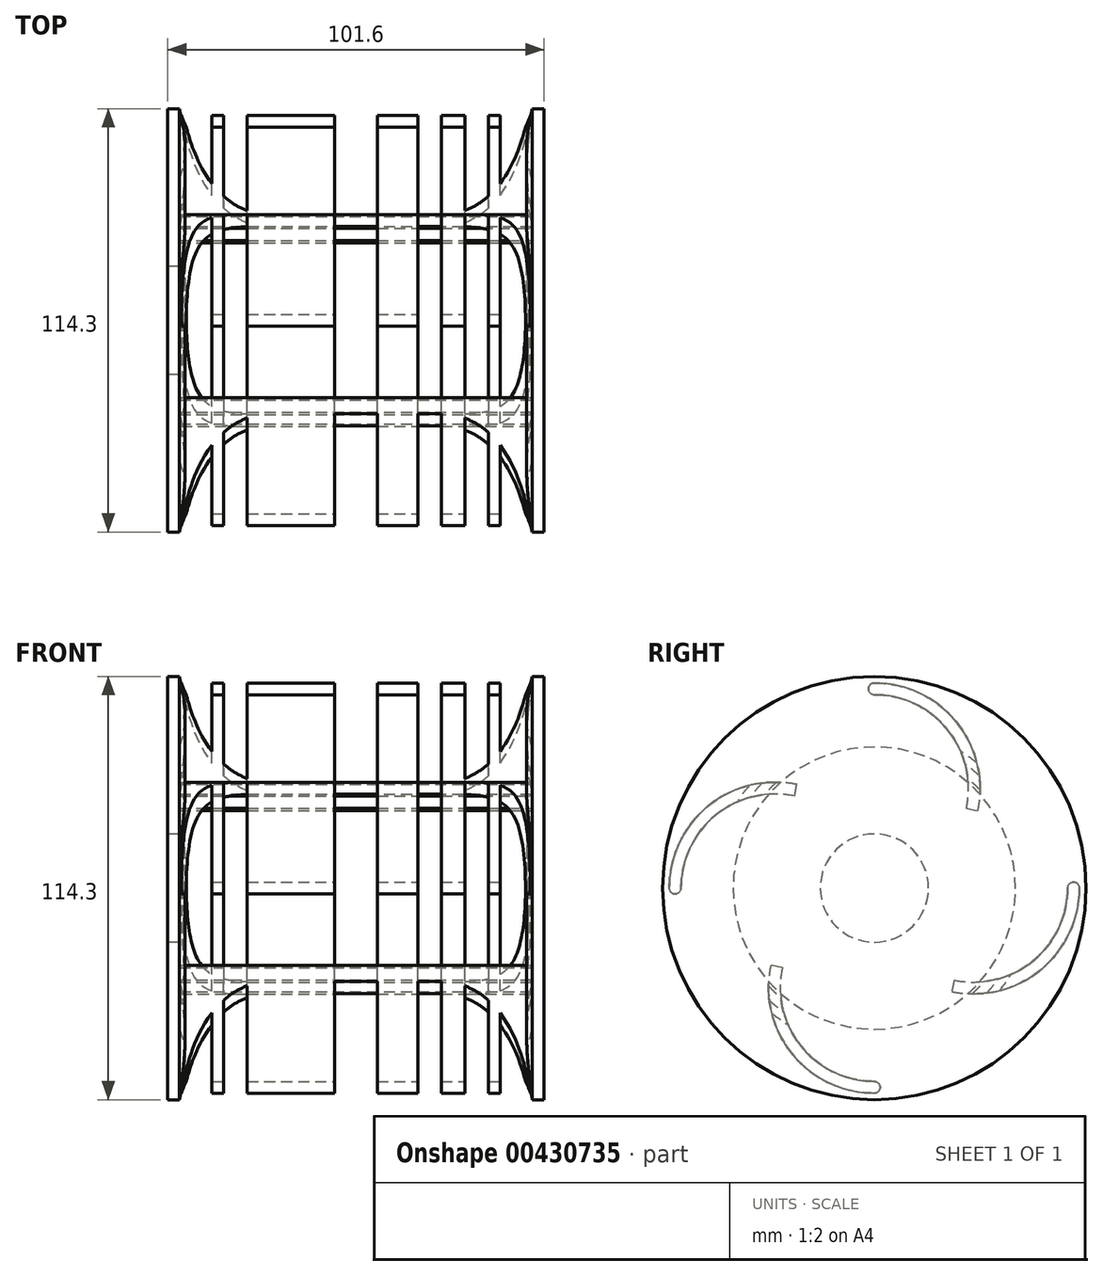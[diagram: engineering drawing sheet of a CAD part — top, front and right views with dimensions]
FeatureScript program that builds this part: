
annotation { "Feature Type Name" : "Feature", "Feature Type Description" : "" }
export const myFeature = defineFeature(function(context is Context, id is Id, definition is map)
    precondition{}
    {
        {
            var Q0;
            Q0=qCreatedBy(makeId("Front.planeOp"),FACE);
            var sketch = newSketch(context, id + "F0", { "sketchPlane" : qUnion([Q0])});
            skLineSegment(sketch, "E0.bottom", {"start": v(0, 0) * mm, "end": v(-101.6, 0) * mm});
            skLineSegment(sketch, "E0.top", {"start": v(0, 38.1) * mm, "end": v(-101.6, 38.1) * mm});
            skLineSegment(sketch, "E0.left", {"start": v(0, 0) * mm, "end": v(0, 38.1) * mm});
            skLineSegment(sketch, "E0.right", {"start": v(-101.6, 0) * mm, "end": v(-101.6, 38.1) * mm});
            skLineSegment(sketch, "E1.bottom", {"start": v(-3.18, 0) * mm, "end": v(0, 0) * mm});
            skLineSegment(sketch, "E1.top", {"start": v(-3.18, 57.15) * mm, "end": v(0, 57.15) * mm});
            skLineSegment(sketch, "E1.left", {"start": v(0, 0) * mm, "end": v(0, 57.15) * mm});
            skLineSegment(sketch, "E1.right", {"start": v(-3.18, 0) * mm, "end": v(-3.18, 57.15) * mm});
            skLineSegment(sketch, "E2.bottom", {"start": v(-101.6, 0) * mm, "end": v(-98.43, 0) * mm});
            skLineSegment(sketch, "E2.top", {"start": v(-101.6, 57.15) * mm, "end": v(-98.43, 57.15) * mm});
            skLineSegment(sketch, "E2.left", {"start": v(-101.6, 0) * mm, "end": v(-101.6, 57.15) * mm});
            skLineSegment(sketch, "E2.right", {"start": v(-98.43, 0) * mm, "end": v(-98.43, 57.15) * mm});
            skLineSegment(sketch, "E3", {"start": v(-98.43, 57.15) * mm, "end": v(-94.62, 38.1) * mm});
            skLineSegment(sketch, "E4", {"start": v(-98.43, 57.15) * mm, "end": v(-98.43, 38.1) * mm});
            skLineSegment(sketch, "E5", {"start": v(-98.43, 38.1) * mm, "end": v(-94.62, 38.1) * mm});
            skLineSegment(sketch, "E6", {"start": v(-3.18, 57.15) * mm, "end": v(-6.99, 38.1) * mm});
            skSolve(sketch);
        }
        {
            var Q0;
            {var subQ0=sQuery(id+"F0.wireOp",EDGE,"E0.bottom");Q0=makeQuery(id+"F0.imprint","IMPRINT",FACE,{"disambiguationData":[TD([[makeQuery(id+"F0.imprint","IMPRINT",EDGE,{"derivedFrom":subQ0}),-1.0]])]});}
            var Q1;
            {var subQ5=sQuery(id+"F0.wireOp",EDGE,"E1.bottom");Q1=makeQuery(id+"F0.imprint","IMPRINT",FACE,{"disambiguationData":[TD([[makeQuery(id+"F0.imprint","IMPRINT",EDGE,{"derivedFrom":subQ5}),1.0]])]});}
            var Q2;
            {var subQ5=sQuery(id+"F0.wireOp",EDGE,"E1.top");Q2=makeQuery(id+"F0.imprint","IMPRINT",FACE,{"disambiguationData":[TD([[makeQuery(id+"F0.imprint","IMPRINT",EDGE,{"derivedFrom":subQ5}),-1.0]])]});}
            var Q3;
            {var subQ5=sQuery(id+"F0.wireOp",EDGE,"E2.top");Q3=makeQuery(id+"F0.imprint","IMPRINT",FACE,{"disambiguationData":[TD([[makeQuery(id+"F0.imprint","IMPRINT",EDGE,{"derivedFrom":subQ5}),-1.0]])]});}
            var Q4;
            {var subQ5=sQuery(id+"F0.wireOp",EDGE,"E2.bottom");Q4=makeQuery(id+"F0.imprint","IMPRINT",FACE,{"disambiguationData":[TD([[makeQuery(id+"F0.imprint","IMPRINT",EDGE,{"derivedFrom":subQ5}),1.0]])]});}
            var Q5;
            Q5=makeQuery(id+"F0.imprint","IMPRINT",FACE,{"disambiguationData":[TD([[makeQuery(id+"F0.imprint","IMPRINT",EDGE,{"derivedFrom":sQuery(id+"F0.wireOp",EDGE,"E3")}),-1.0]])]});
            var Q6;
            {var subQ0=sQuery(id+"F0.wireOp",EDGE,"E6");Q6=makeQuery(id+"F0.imprint","IMPRINT",FACE,{"disambiguationData":[TD([[makeQuery(id+"F0.imprint","IMPRINT",EDGE,{"derivedFrom":subQ0}),1.0]])]});}
            var Q7;
            Q7=sQuery(id+"F0.wireOp",EDGE,"E0.bottom");
            revolve(context, id + "F1", {"entities" : qUnion([Q0, Q1, Q2, Q3, Q4, Q5, Q6]), "axis" : qUnion([Q7]), "revolveType" : RevolveType.FULL});
        }
        {
            var Q0;
            Q0=makeQuery(id+"F1.opRevolve","SWEPT_FACE",FACE,{"disambiguationData":[OSD([sQuery(id+"F0.wireOp",EDGE,"E2.left")])]});
            var sketch = newSketch(context, id + "F2", { "sketchPlane" : qUnion([Q0])});
            skCircle(sketch, "E7.cCircle", {"center": v(0, 0) * mm, "radius": 14.6 * mm});
            skSolve(sketch);
        }
        {
            var Q0;
            Q0=makeQuery(id+"F2.imprint","IMPRINT",FACE,{"disambiguationData":[TD([[makeQuery(id+"F2.imprint","IMPRINT",EDGE,{"derivedFrom":sQuery(id+"F2.wireOp",EDGE,"E7.cCircle")}),1.0]])]});
            extrude(context, id + "F3", {"entities" : qUnion([Q0]), "operationType" : NewBodyOperationType.REMOVE, "endBound" : BoundingType.UP_TO_NEXT, "oppositeDirection" : true, "depth" : 25.4 * mm});
        }
        {
            var Q0;
            Q0=qCreatedBy(makeId("Right.planeOp"),FACE);
            var sketch = newSketch(context, id + "F4", { "sketchPlane" : qUnion([Q0])});
            skArc(sketch, "E8", {"start": v(27.96, 20.9) * mm, "mid": v(22.2, 44.8) * mm, "end": v(0, 55.37) * mm});
            skArc(sketch, "E9.0", {"start": v(24.85, 21.55) * mm, "mid": v(19.73, 42.8) * mm, "end": v(0, 52.2) * mm});
            skArc(sketch, "E10", {"start": v(0, 55.37) * mm, "mid": v(-1.59, 53.78) * mm, "end": v(0, 52.2) * mm});
            skLineSegment(sketch, "E11", {"start": v(24.85, 21.55) * mm, "end": v(27.96, 20.9) * mm});
            skArc(sketch, "E12.1.0", {"start": v(-20.9, 27.96) * mm, "mid": v(-44.8, 22.2) * mm, "end": v(-55.37, 0) * mm});
            skArc(sketch, "E12.1.1", {"start": v(-55.37, 0) * mm, "mid": v(-53.78, -1.59) * mm, "end": v(-52.2, 0) * mm});
            skArc(sketch, "E12.1.2", {"start": v(-21.55, 24.85) * mm, "mid": v(-42.8, 19.73) * mm, "end": v(-52.2, 0) * mm});
            skLineSegment(sketch, "E12.1.3", {"start": v(-21.55, 24.85) * mm, "end": v(-20.9, 27.96) * mm});
            skArc(sketch, "E12.2.0", {"start": v(-27.96, -20.9) * mm, "mid": v(-22.2, -44.8) * mm, "end": v(0, -55.37) * mm});
            skArc(sketch, "E12.2.1", {"start": v(0, -55.37) * mm, "mid": v(1.59, -53.78) * mm, "end": v(0, -52.2) * mm});
            skArc(sketch, "E12.2.2", {"start": v(-24.85, -21.55) * mm, "mid": v(-19.73, -42.8) * mm, "end": v(0, -52.2) * mm});
            skLineSegment(sketch, "E12.2.3", {"start": v(-24.85, -21.55) * mm, "end": v(-27.96, -20.9) * mm});
            skArc(sketch, "E12.3.0", {"start": v(20.9, -27.96) * mm, "mid": v(44.8, -22.2) * mm, "end": v(55.37, 0) * mm});
            skArc(sketch, "E12.3.1", {"start": v(55.37, 0) * mm, "mid": v(53.78, 1.59) * mm, "end": v(52.2, 0) * mm});
            skArc(sketch, "E12.3.2", {"start": v(21.55, -24.85) * mm, "mid": v(42.8, -19.73) * mm, "end": v(52.2, 0) * mm});
            skLineSegment(sketch, "E12.3.3", {"start": v(21.55, -24.85) * mm, "end": v(20.9, -27.96) * mm});
            skPoint(sketch, "E12.center", {"position": v(0, 0) * mm});
            skSolve(sketch);
        }
        {
            var Q0;
            Q0=makeQuery(id+"F1.opRevolve","SWEPT_EDGE",EDGE,{"disambiguationData":[OSD([sQuery(id+"F0.wireOp",EDGE,"E0.top"),sQuery(id+"F0.wireOp",EDGE,"E3"),sQuery(id+"F0.wireOp",EDGE,"E5")])]});
            var Q1;
            Q1=makeQuery(id+"F1.opRevolve","SWEPT_EDGE",EDGE,{"disambiguationData":[OSD([sQuery(id+"F0.wireOp",EDGE,"E0.top"),sQuery(id+"F0.wireOp",EDGE,"E6")])]});
            fillet(context, id + "F5", {"entities" : qUnion([Q0, Q1]), "radius" : 25.4 * mm, "tangentPropagation" : true, "allowEdgeOverflow" : false});
        }
        {
            var Q0;
            Q0=makeQuery(id+"F4.imprint","IMPRINT",FACE,{"disambiguationData":[TD([[makeQuery(id+"F4.imprint","IMPRINT",EDGE,{"derivedFrom":sQuery(id+"F4.wireOp",EDGE,"E8")}),1.0]])]});
            var Q1;
            Q1=makeQuery(id+"F4.imprint","IMPRINT",FACE,{"disambiguationData":[TD([[makeQuery(id+"F4.imprint","IMPRINT",EDGE,{"derivedFrom":sQuery(id+"F4.wireOp",EDGE,"E12.3.0")}),1.0]])]});
            var Q2;
            Q2=makeQuery(id+"F4.imprint","IMPRINT",FACE,{"disambiguationData":[TD([[makeQuery(id+"F4.imprint","IMPRINT",EDGE,{"derivedFrom":sQuery(id+"F4.wireOp",EDGE,"E12.2.0")}),1.0]])]});
            var Q3;
            Q3=makeQuery(id+"F4.imprint","IMPRINT",FACE,{"disambiguationData":[TD([[makeQuery(id+"F4.imprint","IMPRINT",EDGE,{"derivedFrom":sQuery(id+"F4.wireOp",EDGE,"E12.1.0")}),1.0]])]});
            var Q4;
            Q4=makeQuery(id+"F1.opRevolve","SWEPT_FACE",FACE,{"disambiguationData":[OSD([sQuery(id+"F0.wireOp",EDGE,"E2.left")])]});
            extrude(context, id + "F6", {"entities" : qUnion([Q0, Q1, Q2, Q3]), "operationType" : NewBodyOperationType.ADD, "endBound" : BoundingType.UP_TO_SURFACE, "oppositeDirection" : true, "endBoundEntityFace" : qUnion([Q4]), "depth" : 25.4 * mm});
        }
        {
            var Q0;
            Q0=qCreatedBy(makeId("Top.planeOp"),FACE);
            var sketch = newSketch(context, id + "F7", { "sketchPlane" : qUnion([Q0])});
            skArc(sketch, "E13", {"start": v(-73.83, -38.1) * mm, "mid": v(-89.39, -43.42) * mm, "end": v(-98.42, -57.15) * mm});
            skArc(sketch, "E14", {"start": v(-3.18, -57.15) * mm, "mid": v(-12.21, -43.42) * mm, "end": v(-27.77, -38.1) * mm});
            skLineSegment(sketch, "E15", {"start": v(-73.83, -38.1) * mm, "end": v(-27.77, -38.1) * mm});
            skLineSegment(sketch, "E16.bottom", {"start": v(-73.83, -38.1) * mm, "end": v(-67.48, -38.1) * mm});
            skLineSegment(sketch, "E16.top", {"start": v(-73.83, -63.5) * mm, "end": v(-67.48, -63.5) * mm});
            skLineSegment(sketch, "E16.left", {"start": v(-73.83, -38.1) * mm, "end": v(-73.83, -63.5) * mm});
            skLineSegment(sketch, "E16.right", {"start": v(-67.48, -38.1) * mm, "end": v(-67.48, -63.5) * mm});
            skLineSegment(sketch, "E17.left", {"start": v(-56.56, -38.1) * mm, "end": v(-56.56, -63.5) * mm});
            skLineSegment(sketch, "E18", {"start": v(-80.18, -38.9) * mm, "end": v(-80.18, -63.5) * mm});
            skLineSegment(sketch, "E19", {"start": v(-80.18, -63.5) * mm, "end": v(-86.53, -63.5) * mm});
            skLineSegment(sketch, "E20", {"start": v(-86.53, -63.5) * mm, "end": v(-86.53, -41.5) * mm});
            skLineSegment(sketch, "E21", {"start": v(-89.7, -43.67) * mm, "end": v(-89.7, -63.5) * mm});
            skLineSegment(sketch, "E22", {"start": v(-89.7, -63.5) * mm, "end": v(-98.43, -63.5) * mm});
            skLineSegment(sketch, "E23", {"start": v(-98.43, -63.5) * mm, "end": v(-98.43, -57.15) * mm});
            skLineSegment(sketch, "E24", {"start": v(-50.8, -103.16) * mm, "end": v(-50.8, 108.36) * mm, "construction": true});
            skLineSegment(sketch, "E25", {"start": v(-56.56, -63.5) * mm, "end": v(-50.8, -63.5) * mm});
            skLineSegment(sketch, "E26", {"start": v(-50.8, -63.5) * mm, "end": v(-50.8, -38.1) * mm});
            skLineSegment(sketch, "E27", {"start": v(-50.8, -38.1) * mm, "end": v(-56.56, -38.1) * mm});
            skLineSegment(sketch, "E28.MirrorCS", {"start": v(-3.18, -63.5) * mm, "end": v(-3.18, -57.15) * mm});
            skLineSegment(sketch, "E29.MirrorCS", {"start": v(-11.9, -63.5) * mm, "end": v(-3.18, -63.5) * mm});
            skLineSegment(sketch, "E30.MirrorCS", {"start": v(-11.9, -43.67) * mm, "end": v(-11.9, -63.5) * mm});
            skLineSegment(sketch, "E31.MirrorCS", {"start": v(-15.07, -63.5) * mm, "end": v(-15.07, -41.5) * mm});
            skLineSegment(sketch, "E32.MirrorCS", {"start": v(-21.42, -63.5) * mm, "end": v(-15.07, -63.5) * mm});
            skLineSegment(sketch, "E33.MirrorCS", {"start": v(-21.42, -38.9) * mm, "end": v(-21.42, -63.5) * mm});
            skLineSegment(sketch, "E34.MirrorCS", {"start": v(-27.77, -38.1) * mm, "end": v(-27.77, -63.5) * mm});
            skLineSegment(sketch, "E35.MirrorCS", {"start": v(-27.77, -63.5) * mm, "end": v(-34.12, -63.5) * mm});
            skLineSegment(sketch, "E36.MirrorCS", {"start": v(-34.12, -38.1) * mm, "end": v(-34.12, -63.5) * mm});
            skLineSegment(sketch, "E37.MirrorCS", {"start": v(-45.04, -38.1) * mm, "end": v(-45.04, -63.5) * mm});
            skLineSegment(sketch, "E38.MirrorCS", {"start": v(-45.04, -63.5) * mm, "end": v(-50.8, -63.5) * mm});
            skSolve(sketch);
        }
        {
            var Q0;
            {var subQ2=sQuery(id+"F7.wireOp",EDGE,"E21");Q0=makeQuery(id+"F7.imprint","IMPRINT",FACE,{"disambiguationData":[TD([[makeQuery(id+"F7.imprint","IMPRINT",EDGE,{"derivedFrom":subQ2}),-1.0]])]});}
            var Q1;
            {var subQ0=sQuery(id+"F7.wireOp",EDGE,"E18");Q1=makeQuery(id+"F7.imprint","IMPRINT",FACE,{"disambiguationData":[TD([[makeQuery(id+"F7.imprint","IMPRINT",EDGE,{"derivedFrom":subQ0}),-1.0]])]});}
            var Q2;
            Q2=makeQuery(id+"F7.imprint","IMPRINT",FACE,{"disambiguationData":[TD([[makeQuery(id+"F7.imprint","IMPRINT",EDGE,{"derivedFrom":sQuery(id+"F7.wireOp",EDGE,"E16.bottom")}),-1.0]])]});
            var Q3;
            Q3=makeQuery(id+"F7.imprint","IMPRINT",FACE,{"disambiguationData":[TD([[makeQuery(id+"F7.imprint","IMPRINT",EDGE,{"derivedFrom":sQuery(id+"F7.wireOp",EDGE,"E17.left")}),1.0]])]});
            var Q4;
            {var subQ0=sQuery(id+"F7.wireOp",EDGE,"E26");Q4=makeQuery(id+"F7.imprint","IMPRINT",FACE,{"disambiguationData":[TD([[makeQuery(id+"F7.imprint","IMPRINT",EDGE,{"derivedFrom":subQ0}),-1.0]])]});}
            var Q5;
            {var subQ0=sQuery(id+"F7.wireOp",EDGE,"E34.MirrorCS");Q5=makeQuery(id+"F7.imprint","IMPRINT",FACE,{"disambiguationData":[TD([[makeQuery(id+"F7.imprint","IMPRINT",EDGE,{"derivedFrom":subQ0}),-1.0]])]});}
            var Q6;
            {var subQ0=sQuery(id+"F7.wireOp",EDGE,"E31.MirrorCS");Q6=makeQuery(id+"F7.imprint","IMPRINT",FACE,{"disambiguationData":[TD([[makeQuery(id+"F7.imprint","IMPRINT",EDGE,{"derivedFrom":subQ0}),1.0]])]});}
            var Q7;
            {var subQ0=sQuery(id+"F7.wireOp",EDGE,"E28.MirrorCS");Q7=makeQuery(id+"F7.imprint","IMPRINT",FACE,{"disambiguationData":[TD([[makeQuery(id+"F7.imprint","IMPRINT",EDGE,{"derivedFrom":subQ0}),1.0]])]});}
            var Q8;
            Q8=makeQuery(id+"F3.boolean.opBoolean","COPY",FACE,{"derivedFrom":makeQuery(id+"F3.opExtrude","SWEPT_FACE",FACE,{"disambiguationData":[OSD([sQuery(id+"F2.wireOp",EDGE,"E7.cCircle")])]})});
            revolve(context, id + "F8", {"operationType" : NewBodyOperationType.REMOVE, "entities" : qUnion([Q0, Q1, Q2, Q3, Q4, Q5, Q6, Q7]), "axis" : qUnion([Q8]), "revolveType" : RevolveType.FULL, "oppositeDirection" : true});
        }
    });
